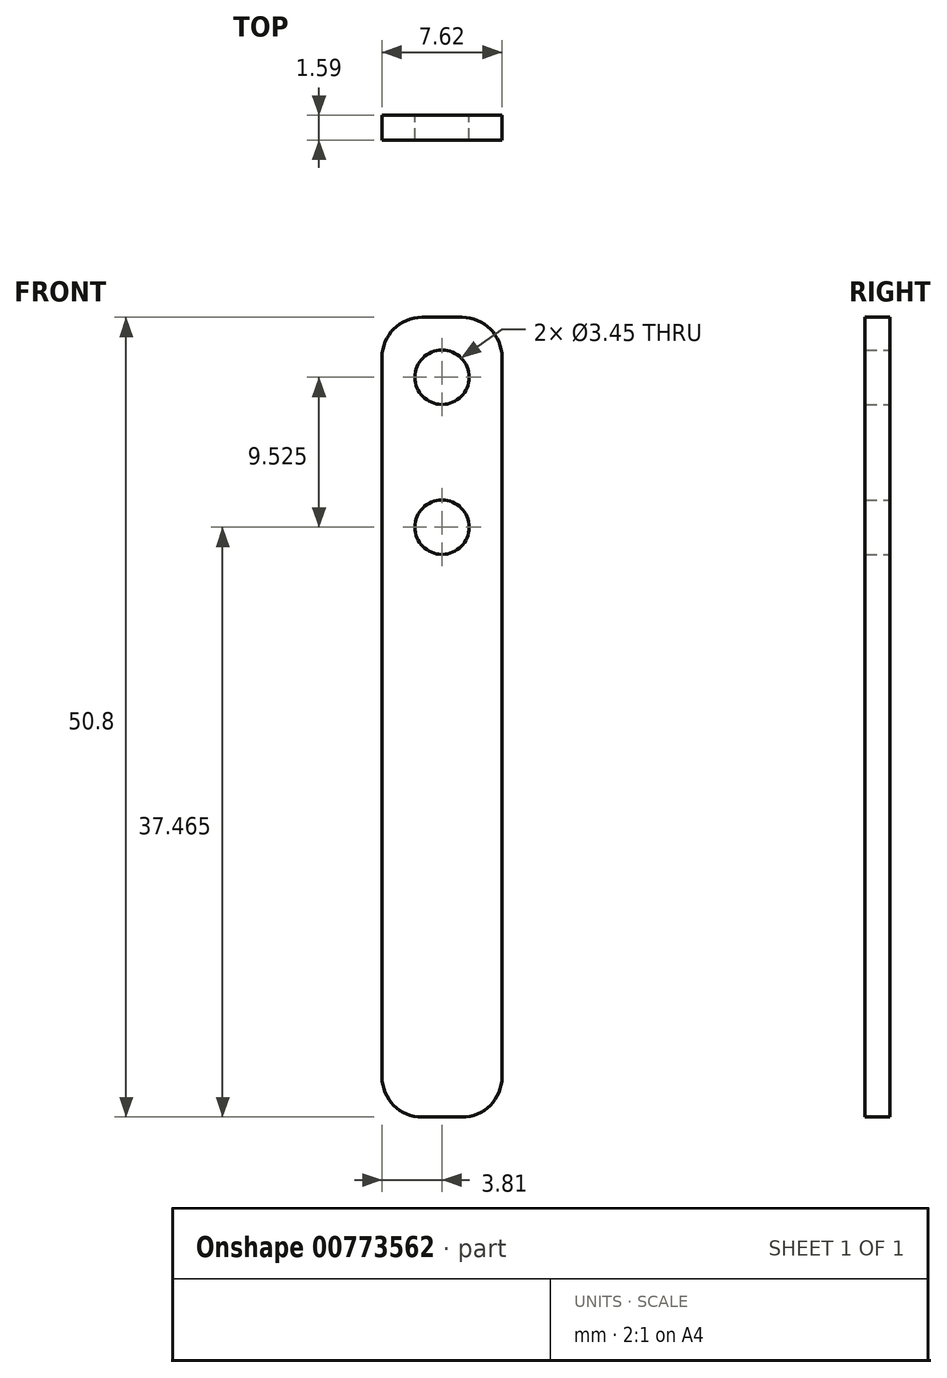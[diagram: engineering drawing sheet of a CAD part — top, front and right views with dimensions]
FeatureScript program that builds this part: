
annotation { "Feature Type Name" : "Feature", "Feature Type Description" : "" }
export const myFeature = defineFeature(function(context is Context, id is Id, definition is map)
    precondition{}
    {
        {
            var Q0;
            Q0=qCreatedBy(makeId("Front.planeOp"),FACE);
            var sketch = newSketch(context, id + "F0", { "sketchPlane" : qUnion([Q0])});
            skLineSegment(sketch, "E0.bottom", {"start": v(2.54, 0) * mm, "end": v(5.08, 0) * mm});
            skLineSegment(sketch, "E0.top", {"start": v(2.54, -50.8) * mm, "end": v(5.08, -50.8) * mm});
            skLineSegment(sketch, "E0.left", {"start": v(0, -2.54) * mm, "end": v(0, -48.26) * mm});
            skLineSegment(sketch, "E0.right", {"start": v(7.62, -2.54) * mm, "end": v(7.62, -48.26) * mm});
            skLineSegment(sketch, "E1", {"start": v(3.8, 0) * mm, "end": v(3.81, -50.8) * mm, "construction": true});
            skPoint(sketch, "E2.visualSharp", {"position": v(0, 0) * mm});
            skArc(sketch, "E2.filletArc", {"start": v(2.54, 0) * mm, "mid": v(0.74, -0.74) * mm, "end": v(0, -2.54) * mm});
            skPoint(sketch, "E3.visualSharp", {"position": v(7.62, 0) * mm});
            skArc(sketch, "E3.filletArc", {"start": v(7.62, -2.54) * mm, "mid": v(6.88, -0.74) * mm, "end": v(5.08, 0) * mm});
            skPoint(sketch, "E4.visualSharp", {"position": v(0, -50.8) * mm});
            skArc(sketch, "E4.filletArc", {"start": v(0, -48.26) * mm, "mid": v(0.74, -50.06) * mm, "end": v(2.54, -50.8) * mm});
            skPoint(sketch, "E5.visualSharp", {"position": v(7.62, -50.8) * mm});
            skArc(sketch, "E5.filletArc", {"start": v(5.08, -50.8) * mm, "mid": v(6.88, -50.06) * mm, "end": v(7.62, -48.26) * mm});
            skSolve(sketch);
        }
        {
            var Q0;
            Q0 = qSketchRegion(id + "F0", true);
            extrude(context, id + "F1", {"entities" : qUnion([Q0]), "depth" : 1.59 * mm, "offsetDistance" : 25.4 * mm});
        }
        {
            var Q0;
            Q0=qCreatedBy(makeId("Front.planeOp"),FACE);
            var sketch = newSketch(context, id + "F2", { "sketchPlane" : qUnion([Q0])});
            skCircle(sketch, "E6", {"center": v(3.8, -3.81) * mm, "radius": 1.73 * mm});
            skCircle(sketch, "E7", {"center": v(3.8, -13.34) * mm, "radius": 1.73 * mm});
            skSolve(sketch);
        }
        {
            var Q0;
            Q0 = qSketchRegion(id + "F2", true);
            extrude(context, id + "F3", {"entities" : qUnion([Q0]), "operationType" : NewBodyOperationType.REMOVE, "endBound" : BoundingType.THROUGH_ALL, "depth" : 25.4 * mm, "offsetDistance" : 25.4 * mm});
        }
    });
